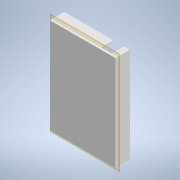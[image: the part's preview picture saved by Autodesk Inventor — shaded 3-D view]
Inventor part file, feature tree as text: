
AUTODESK INVENTOR PART (.ipt)
format: ipt  version: 2020 (Build 240168000, 168)  size: 165,888 bytes
history: native  units: in
note: dims shown in document units (in); Inventor stores cm internally (conversion verified against a paired STEP export)
features: extrude x6, sketch x6, other x3, plane x1
ambient origin geometry x8: Origin, YZ Plane, XZ Plane, XY Plane, X Axis, Y Axis, Z Axis, Center Point
bodies: Solid1 (feature_tree)
feature tree (16):
  plane  "Work Plane1"
  extrude  "Extrusion1"  Depth=0.0232in TaperAngle=0.0deg
  extrude  "Extrusion2"  Depth=0.3937in TaperAngle=0.0deg
  extrude  "Extrusion3"  Depth=0.0591in
  extrude  "Extrusion4"  Depth=0.0591in
  extrude  "Extrusion6"  Depth=0.1772in TaperAngle=0.0deg
  extrude  "Extrusion5"  Depth=0.0344in
  sketch  "Sketch1"  dims[d0=0.0812in d1=0.5719in d2=0.0in d3=0.0in d4=0.0232in d5=0.0in]
  sketch  "Sketch2"  dims[d6=0.0232in d7=0.0in d8=0.3937in d9=0.0in]
  sketch  "Sketch3"  dims[d10=0.1772in d11=0.0in d12=0.0591in]
  sketch  "Sketch4"  dims[d13=0.0591in d14=0.0591in]
  sketch  "Sketch5"  dims[d15=0.0591in d16=0.1772in d17=0.0in]
  sketch  "Sketch6"  dims[d18=0.0197in d19=0.0344in]
  parser-record x1  (decoder bookkeeping rows leaked as tree rows — omitted from the tree; the rows remain in map.json)
  other  "I0020.iam"
  other  "Buttom Case:1"
note: 1 file-system path scrubbed to <path> (originals preserved in map.json)
